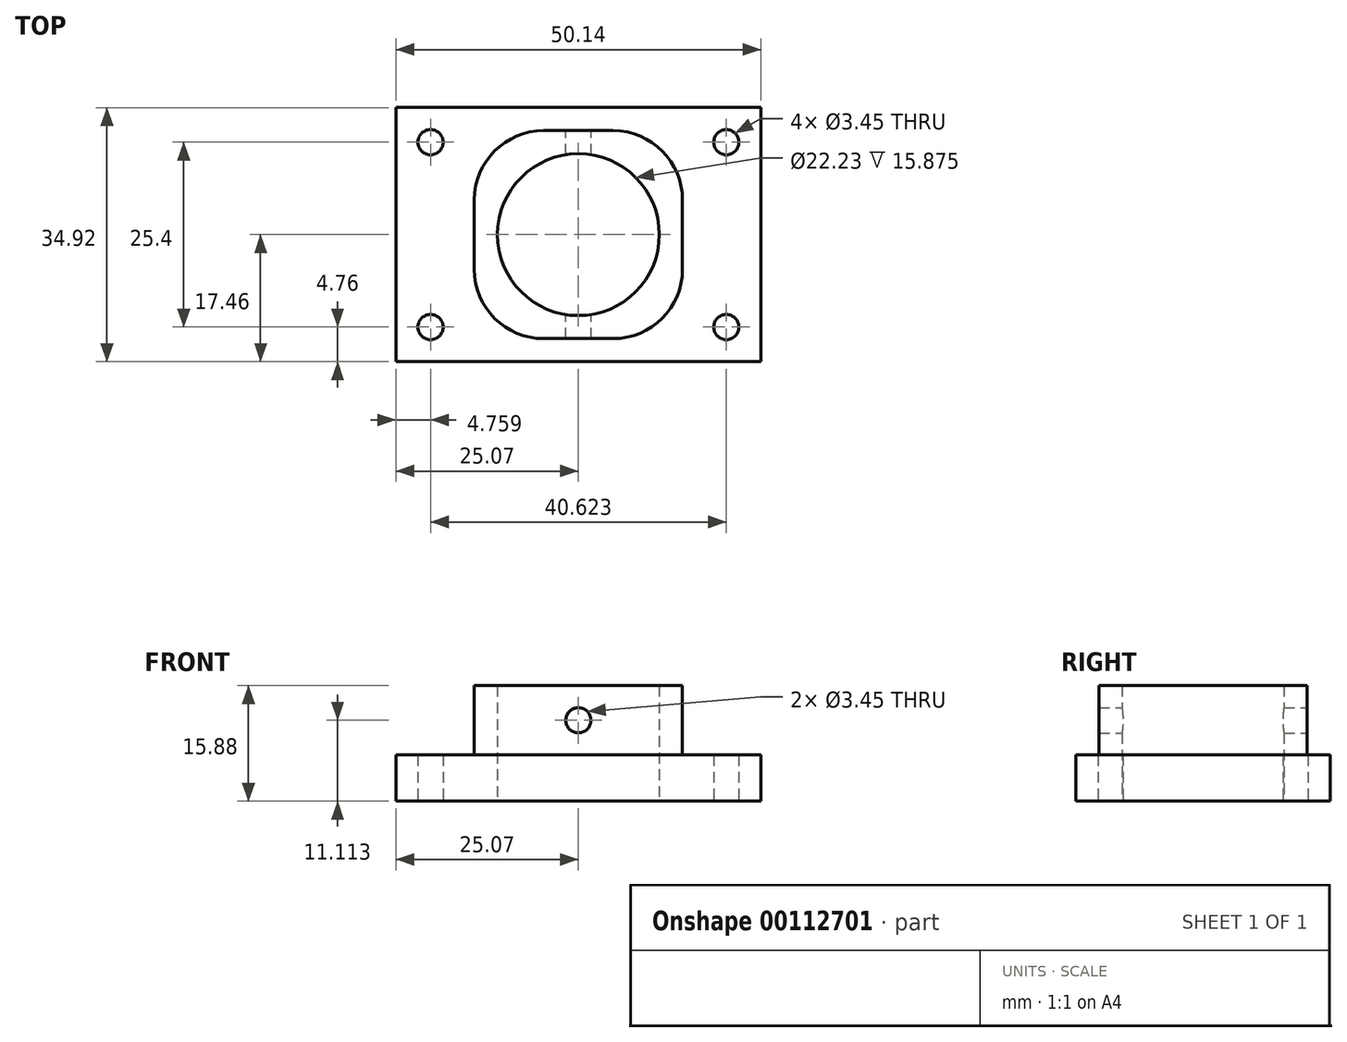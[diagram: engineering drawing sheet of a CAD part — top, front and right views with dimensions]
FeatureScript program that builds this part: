
annotation { "Feature Type Name" : "Feature", "Feature Type Description" : "" }
export const myFeature = defineFeature(function(context is Context, id is Id, definition is map)
    precondition{}
    {
        {
            var Q0;
            Q0=qCreatedBy(makeId("Top.planeOp"),FACE);
            var sketch = newSketch(context, id + "F0", { "sketchPlane" : qUnion([Q0])});
            skCircle(sketch, "E0", {"center": v(0, 0) * mm, "radius": 11.11 * mm});
            skLineSegment(sketch, "E1.bottom", {"start": v(25.07, 17.46) * mm, "end": v(-25.07, 17.46) * mm});
            skLineSegment(sketch, "E1.top", {"start": v(25.07, -17.46) * mm, "end": v(-25.07, -17.46) * mm});
            skLineSegment(sketch, "E1.left", {"start": v(25.07, 17.46) * mm, "end": v(25.07, -17.46) * mm});
            skLineSegment(sketch, "E1.right", {"start": v(-25.07, 17.46) * mm, "end": v(-25.07, -17.46) * mm});
            skLineSegment(sketch, "E2.bottom", {"start": v(20.31, 12.7) * mm, "end": v(-20.31, 12.7) * mm, "construction": true});
            skLineSegment(sketch, "E2.top", {"start": v(20.31, -12.7) * mm, "end": v(-20.31, -12.7) * mm, "construction": true});
            skLineSegment(sketch, "E2.left", {"start": v(20.31, 12.7) * mm, "end": v(20.31, -12.7) * mm, "construction": true});
            skLineSegment(sketch, "E2.right", {"start": v(-20.31, 12.7) * mm, "end": v(-20.31, -12.7) * mm, "construction": true});
            skLineSegment(sketch, "E3", {"start": v(20.31, 12.7) * mm, "end": v(20.31, 17.46) * mm, "construction": true});
            skLineSegment(sketch, "E4", {"start": v(20.31, 12.7) * mm, "end": v(25.07, 12.7) * mm, "construction": true});
            skCircle(sketch, "E5", {"center": v(-20.31, 12.7) * mm, "radius": 1.73 * mm});
            skCircle(sketch, "E6", {"center": v(20.31, 12.7) * mm, "radius": 1.73 * mm});
            skCircle(sketch, "E7", {"center": v(20.31, -12.7) * mm, "radius": 1.73 * mm});
            skCircle(sketch, "E8", {"center": v(-20.31, -12.7) * mm, "radius": 1.73 * mm});
            skSolve(sketch);
        }
        {
            var Q0;
            Q0 = qSketchRegion(id + "F0", true);
            extrude(context, id + "F1", {"entities" : qUnion([Q0]), "depth" : 6.35 * mm});
        }
        {
            var Q0;
            Q0=makeQuery(id+"F1.opExtrude","CAP_FACE",FACE,{"disambiguationData":[OSD([sQuery(id+"F0.wireOp",EDGE,"E0"),sQuery(id+"F0.wireOp",EDGE,"E1.bottom"),sQuery(id+"F0.wireOp",EDGE,"E1.top"),sQuery(id+"F0.wireOp",EDGE,"E1.left"),sQuery(id+"F0.wireOp",EDGE,"E1.right"),sQuery(id+"F0.wireOp",EDGE,"E5"),sQuery(id+"F0.wireOp",EDGE,"E6"),sQuery(id+"F0.wireOp",EDGE,"E7"),sQuery(id+"F0.wireOp",EDGE,"E8")])],"isStart":false});
            var sketch = newSketch(context, id + "F2", { "sketchPlane" : qUnion([Q0])});
            skLineSegment(sketch, "E9.bottom", {"start": v(14.29, 14.29) * mm, "end": v(-14.29, 14.29) * mm});
            skLineSegment(sketch, "E9.top", {"start": v(14.29, -14.29) * mm, "end": v(-14.29, -14.29) * mm});
            skLineSegment(sketch, "E9.left", {"start": v(14.29, 14.29) * mm, "end": v(14.29, -14.29) * mm});
            skLineSegment(sketch, "E9.right", {"start": v(-14.29, 14.29) * mm, "end": v(-14.29, -14.29) * mm});
            skPoint(sketch, "E9.middle", {"position": v(0, 0) * mm});
            skCircle(sketch, "E10", {"center": v(0, 0) * mm, "radius": 11.11 * mm});
            skSolve(sketch);
        }
        {
            var Q0;
            Q0 = qSketchRegion(id + "F2", true);
            extrude(context, id + "F3", {"entities" : qUnion([Q0]), "operationType" : NewBodyOperationType.ADD, "depth" : 9.52 * mm});
        }
        {
            var Q0;
            Q0=makeQuery(id+"F3.opExtrude","SWEPT_FACE",FACE,{"disambiguationData":[OSD([sQuery(id+"F2.wireOp",EDGE,"E9.bottom")])]});
            var sketch = newSketch(context, id + "F4", { "sketchPlane" : qUnion([Q0])});
            skLineSegment(sketch, "E11", {"start": v(0, 15.88) * mm, "end": v(0, 6.35) * mm, "construction": true});
            skCircle(sketch, "E12", {"center": v(0, 11.11) * mm, "radius": 1.73 * mm});
            skSolve(sketch);
        }
        {
            var Q0;
            Q0 = qSketchRegion(id + "F4", true);
            var Q1;
            Q1=makeQuery(id+"F3.opExtrude","SWEPT_FACE",FACE,{"disambiguationData":[OSD([sQuery(id+"F2.wireOp",EDGE,"E9.top")])]});
            extrude(context, id + "F5", {"entities" : qUnion([Q0]), "operationType" : NewBodyOperationType.REMOVE, "endBound" : BoundingType.UP_TO_SURFACE, "oppositeDirection" : true, "endBoundEntityFace" : qUnion([Q1]), "depth" : 25.4 * mm});
        }
        {
            var Q0;
            Q0=makeQuery(id+"F3.opExtrude","SWEPT_EDGE",EDGE,{"disambiguationData":[OSD([sQuery(id+"F2.wireOp",EDGE,"E9.top"),sQuery(id+"F2.wireOp",EDGE,"E9.right")])]});
            var Q1;
            Q1=makeQuery(id+"F3.opExtrude","SWEPT_EDGE",EDGE,{"disambiguationData":[OSD([sQuery(id+"F2.wireOp",EDGE,"E9.top"),sQuery(id+"F2.wireOp",EDGE,"E9.left")])]});
            var Q2;
            Q2=makeQuery(id+"F3.opExtrude","SWEPT_EDGE",EDGE,{"disambiguationData":[OSD([sQuery(id+"F2.wireOp",EDGE,"E9.bottom"),sQuery(id+"F2.wireOp",EDGE,"E9.left")])]});
            var Q3;
            Q3=makeQuery(id+"F3.opExtrude","SWEPT_EDGE",EDGE,{"disambiguationData":[OSD([sQuery(id+"F2.wireOp",EDGE,"E9.bottom"),sQuery(id+"F2.wireOp",EDGE,"E9.right")])]});
            fillet(context, id + "F6", {"entities" : qUnion([Q0, Q1, Q2, Q3]), "radius" : 9.52 * mm, "tangentPropagation" : true, "allowEdgeOverflow" : false});
        }
    });
